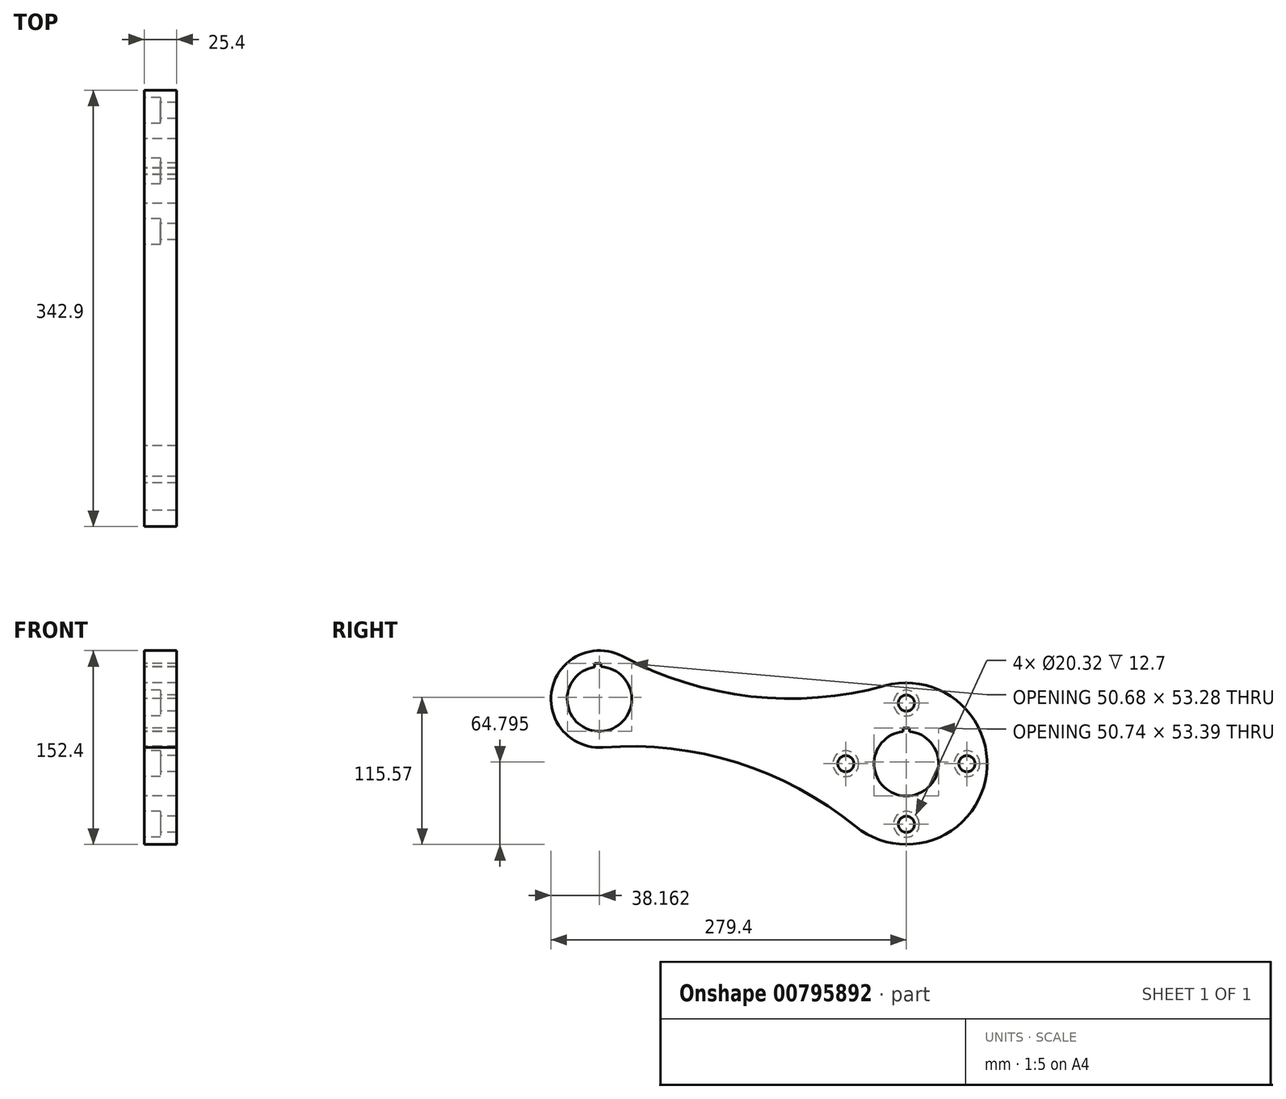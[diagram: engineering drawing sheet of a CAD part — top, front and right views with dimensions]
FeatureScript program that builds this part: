
annotation { "Feature Type Name" : "Feature", "Feature Type Description" : "" }
export const myFeature = defineFeature(function(context is Context, id is Id, definition is map)
    precondition{}
    {
        {
            var Q0;
            Q0=qCreatedBy(makeId("Right.planeOp"),FACE);
            var sketch = newSketch(context, id + "F0", { "sketchPlane" : qUnion([Q0])});
            skArc(sketch, "E0.0", {"start": v(-2.54, 25.27) * mm, "mid": v(0, -25.4) * mm, "end": v(2.55, 25.27) * mm});
            skCircle(sketch, "E1", {"center": v(0, 0) * mm, "radius": 63.5 * mm});
            skCircle(sketch, "E2.converted", {"center": v(-241.3, 50.8) * mm, "radius": 38.1 * mm});
            skArc(sketch, "E3", {"start": v(-223.28, 84.37) * mm, "mid": v(-122.31, 52.9) * mm, "end": v(-16.88, 61.21) * mm});
            skArc(sketch, "E4", {"start": v(-40.13, -49.21) * mm, "mid": v(-133.26, 0.9) * mm, "end": v(-238.35, 12.81) * mm});
            skPoint(sketch, "E5.middle", {"position": v(-242.52, 76.17) * mm});
            skPoint(sketch, "E5.top.end.orphan", {"position": v(-246.71, 73.63) * mm});
            skPoint(sketch, "E6.orphan", {"position": v(-238.1, 60.95) * mm});
            skLineSegment(sketch, "E7.bottom", {"start": v(2.39, 27.9) * mm, "end": v(-2.71, 27.99) * mm});
            skLineSegment(sketch, "E7.left", {"start": v(2.39, 27.9) * mm, "end": v(2.55, 25.27) * mm});
            skLineSegment(sketch, "E7.right", {"start": v(-2.71, 27.99) * mm, "end": v(-2.54, 25.27) * mm});
            skPoint(sketch, "E7.middle", {"position": v(0, 25.4) * mm});
            skPoint(sketch, "E8.orphan", {"position": v(2.71, 22.81) * mm});
            skPoint(sketch, "E9.orphan", {"position": v(-2.39, 22.9) * mm});
            skArc(sketch, "E10.converted", {"start": v(-245.06, 75.92) * mm, "mid": v(-240.07, 25.43) * mm, "end": v(-239.98, 76.17) * mm});
            skCircle(sketch, "E11", {"center": v(0, 0) * mm, "radius": 47.63 * mm, "construction": true});
            skCircle(sketch, "E12", {"center": v(0, 47.62) * mm, "radius": 6.35 * mm});
            skCircle(sketch, "E13", {"center": v(0, -47.63) * mm, "radius": 6.35 * mm});
            skLineSegment(sketch, "E14.top", {"start": v(-245.06, 78.71) * mm, "end": v(-239.98, 78.71) * mm});
            skLineSegment(sketch, "E14.left", {"start": v(-245.06, 75.92) * mm, "end": v(-245.06, 78.71) * mm});
            skLineSegment(sketch, "E14.right", {"start": v(-239.98, 76.17) * mm, "end": v(-239.98, 78.71) * mm});
            skPoint(sketch, "E15.orphan", {"position": v(-239.98, 73.63) * mm});
            skPoint(sketch, "E16.orphan", {"position": v(-245.06, 73.63) * mm});
            skCircle(sketch, "E17", {"center": v(-47.63, 0) * mm, "radius": 6.35 * mm});
            skCircle(sketch, "E18", {"center": v(47.63, 0) * mm, "radius": 6.35 * mm});
            skSolve(sketch);
        }
        {
            var Q0;
            Q0 = qSketchRegion(id + "F0", true);
            extrude(context, id + "F1", {"entities" : qUnion([Q0]), "depth" : 25.4 * mm, "offsetDistance" : 25.4 * mm});
        }
        {
            var Q0;
            Q0=makeQuery(id+"F1.opExtrude","CAP_FACE",FACE,{"disambiguationData":[OSD([sQuery(id+"F0.wireOp",EDGE,"E0.0"),sQuery(id+"F0.wireOp",EDGE,"E1"),sQuery(id+"F0.wireOp",EDGE,"E2.converted"),sQuery(id+"F0.wireOp",EDGE,"E3"),sQuery(id+"F0.wireOp",EDGE,"E4"),sQuery(id+"F0.wireOp",EDGE,"E7.bottom"),sQuery(id+"F0.wireOp",EDGE,"E7.left"),sQuery(id+"F0.wireOp",EDGE,"E7.right"),sQuery(id+"F0.wireOp",EDGE,"E10.converted"),sQuery(id+"F0.wireOp",EDGE,"E12"),sQuery(id+"F0.wireOp",EDGE,"E13"),sQuery(id+"F0.wireOp",EDGE,"E14.top"),sQuery(id+"F0.wireOp",EDGE,"E14.left"),sQuery(id+"F0.wireOp",EDGE,"E14.right")])],"isStart":true});
            var sketch = newSketch(context, id + "F2", { "sketchPlane" : qUnion([Q0])});
            skSolve(sketch);
        }
        {
            var Q0;
            Q0=makeQuery(id+"F2.imprint","IMPRINT",FACE,{"disambiguationData":[TD([[makeQuery(id+"F2.imprint","IMPRINT",EDGE,{"derivedFrom":makeQuery(id+"F1.opExtrude","CAP_EDGE",EDGE,{"disambiguationData":[OSD([sQuery(id+"F0.wireOp",EDGE,"E0.0")])],"isStart":true})}),1.0]])]});
            var sketch = newSketch(context, id + "F3", { "sketchPlane" : qUnion([Q0])});
            skCircle(sketch, "E19", {"center": v(0, 0) * mm, "radius": 47.63 * mm, "construction": true});
            skCircle(sketch, "E20", {"center": v(0, 47.63) * mm, "radius": 10.16 * mm});
            skCircle(sketch, "E21", {"center": v(47.63, 0) * mm, "radius": 10.16 * mm});
            skCircle(sketch, "E22", {"center": v(0, -47.63) * mm, "radius": 10.16 * mm});
            skCircle(sketch, "E23", {"center": v(-47.63, 0) * mm, "radius": 10.16 * mm});
            skSolve(sketch);
        }
        {
            var Q0;
            Q0 = qSketchRegion(id + "F3", true);
            extrude(context, id + "F4", {"entities" : qUnion([Q0]), "operationType" : NewBodyOperationType.REMOVE, "oppositeDirection" : true, "depth" : 12.7 * mm, "offsetDistance" : 25.4 * mm});
        }
    });
